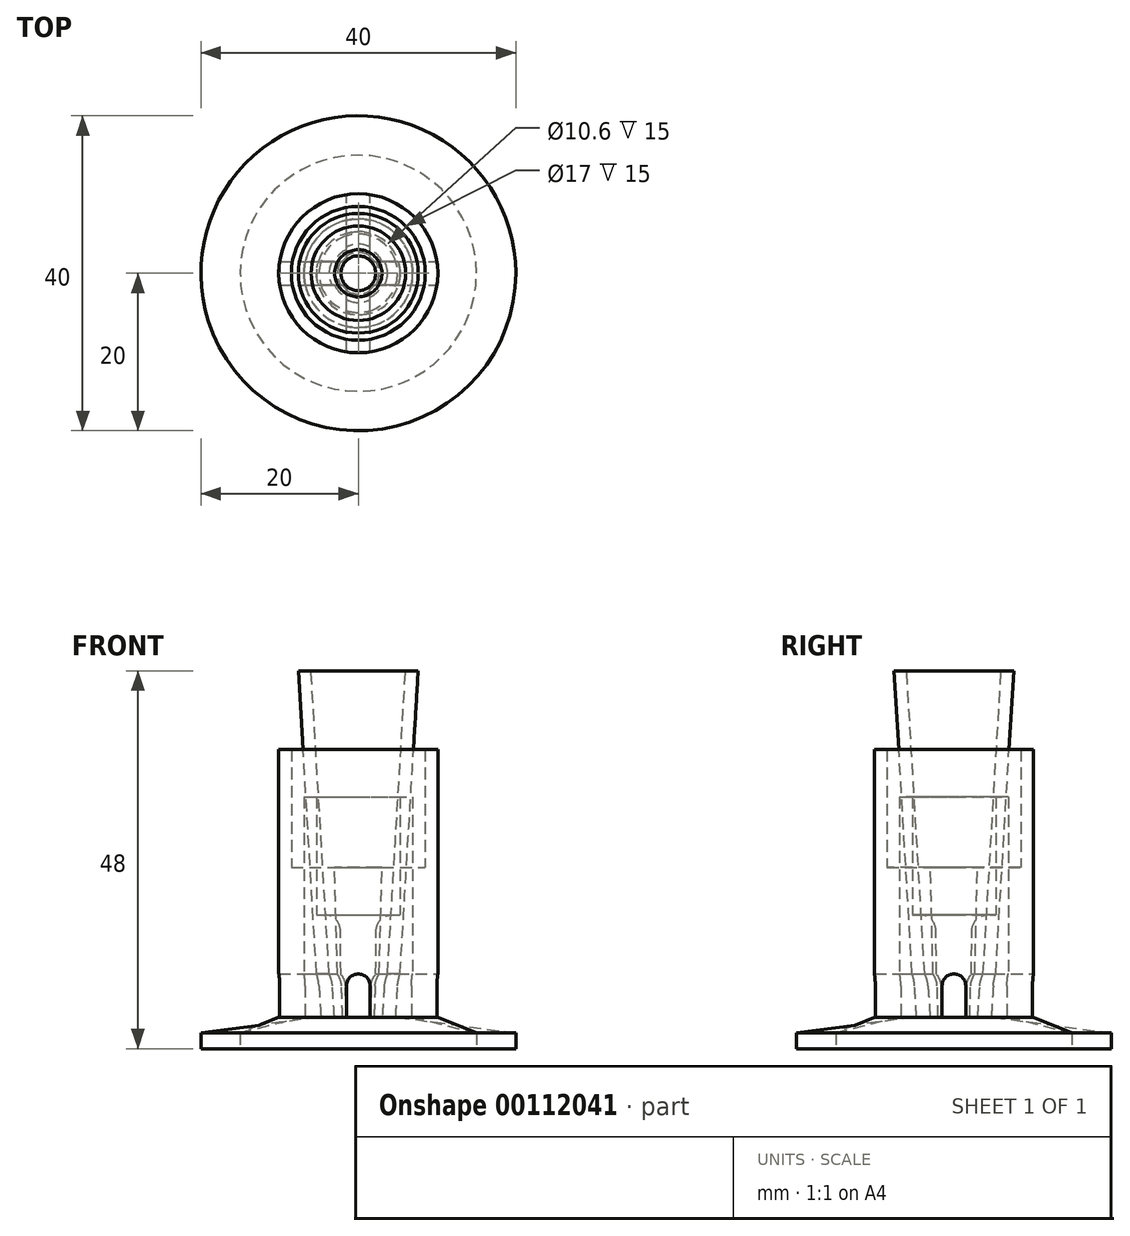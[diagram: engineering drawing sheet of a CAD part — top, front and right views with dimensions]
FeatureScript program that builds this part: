
annotation { "Feature Type Name" : "Feature", "Feature Type Description" : "" }
export const myFeature = defineFeature(function(context is Context, id is Id, definition is map)
    precondition{}
    {
        {
            var Q0;
            Q0=qCreatedBy(makeId("Front.planeOp"),FACE);
            var sketch = newSketch(context, id + "F0", { "sketchPlane" : qUnion([Q0])});
            skLineSegment(sketch, "E0", {"start": v(0, 0) * mm, "end": v(20, 0) * mm});
            skLineSegment(sketch, "E1", {"start": v(20, 0) * mm, "end": v(20, 2) * mm});
            skLineSegment(sketch, "E2", {"start": v(20, 2) * mm, "end": v(4.98, 4) * mm});
            skLineSegment(sketch, "E3", {"start": v(4.98, 4) * mm, "end": v(7.6, 48) * mm});
            skLineSegment(sketch, "E4", {"start": v(7.6, 48) * mm, "end": v(6, 48) * mm});
            skLineSegment(sketch, "E5", {"start": v(6, 48) * mm, "end": v(3.38, 4) * mm});
            skLineSegment(sketch, "E6", {"start": v(3.38, 4) * mm, "end": v(0, 4) * mm});
            skLineSegment(sketch, "E7", {"start": v(0, 4) * mm, "end": v(0, 0) * mm});
            skPoint(sketch, "E8", {"position": v(3.5, 6) * mm});
            skSolve(sketch);
        }
        {
            var Q0;
            Q0 = qSketchRegion(id + "F0", true);
            var Q1;
            Q1=sQuery(id+"F0.wireOp",EDGE,"E7");
            revolve(context, id + "F1", {"entities" : qUnion([Q0]), "axis" : qUnion([Q1]), "revolveType" : RevolveType.FULL});
        }
        {
            var Q0;
            Q0=qCreatedBy(makeId("Front.planeOp"),FACE);
            var sketch = newSketch(context, id + "F2", { "sketchPlane" : qUnion([Q0])});
            skLineSegment(sketch, "E9", {"start": v(1.5, 4) * mm, "end": v(-1.5, 4) * mm});
            skLineSegment(sketch, "E10", {"start": v(-1.5, 4) * mm, "end": v(-1.5, 8) * mm});
            skLineSegment(sketch, "E11", {"start": v(1.5, 4) * mm, "end": v(1.5, 8) * mm});
            skArc(sketch, "E12", {"start": v(1.5, 8) * mm, "mid": v(0, 9.5) * mm, "end": v(-1.5, 8) * mm});
            skSolve(sketch);
        }
        {
            var Q0;
            Q0 = qSketchRegion(id + "F2", true);
            extrude(context, id + "F3", {"entities" : qUnion([Q0]), "endBound" : BoundingType.SYMMETRIC, "depth" : 20 * mm});
        }
        {
            var Q0;
            Q0=makeQuery(id+"F3.opExtrude","SWEPT_BODY",BODY,{"disambiguationData":[OSD([sQuery(id+"F2.wireOp",EDGE,"E9"),sQuery(id+"F2.wireOp",EDGE,"E10"),sQuery(id+"F2.wireOp",EDGE,"E11"),sQuery(id+"F2.wireOp",EDGE,"E12")])]});
            var Q1;
            Q1=makeQuery(id+"F1.opRevolve","SWEPT_EDGE",EDGE,{"disambiguationData":[OSD([sQuery(id+"F0.wireOp",EDGE,"E4"),sQuery(id+"F0.wireOp",EDGE,"E5")])]});
            transform(context, id + "F4", {"entities" : qUnion([Q0]), "transformType" : TransformType.ROTATION, "transformAxis" : qUnion([Q1]), "angle" : 90 * degree, "makeCopy" : true});
        }
        {
            var Q0;
            Q0=makeQuery(id+"F3.opExtrude","SWEPT_BODY",BODY,{"disambiguationData":[OSD([sQuery(id+"F2.wireOp",EDGE,"E9"),sQuery(id+"F2.wireOp",EDGE,"E10"),sQuery(id+"F2.wireOp",EDGE,"E11"),sQuery(id+"F2.wireOp",EDGE,"E12")])]});
            var Q1;
            Q1=makeQuery(id+"F4.opPattern","COPY",BODY,{"derivedFrom":makeQuery(id+"F3.opExtrude","SWEPT_BODY",BODY,{"disambiguationData":[OSD([sQuery(id+"F2.wireOp",EDGE,"E9"),sQuery(id+"F2.wireOp",EDGE,"E10"),sQuery(id+"F2.wireOp",EDGE,"E11"),sQuery(id+"F2.wireOp",EDGE,"E12")])]}),"instanceName":"1"});
            var Q2;
            Q2=makeQuery(id+"F1.opRevolve","SWEPT_BODY",BODY,{"disambiguationData":[OSD([sQuery(id+"F0.wireOp",EDGE,"E0"),sQuery(id+"F0.wireOp",EDGE,"E1"),sQuery(id+"F0.wireOp",EDGE,"E2"),sQuery(id+"F0.wireOp",EDGE,"E3"),sQuery(id+"F0.wireOp",EDGE,"E4"),sQuery(id+"F0.wireOp",EDGE,"E5"),sQuery(id+"F0.wireOp",EDGE,"E6"),sQuery(id+"F0.wireOp",EDGE,"E7")])]});
            booleanBodies(context, id + "F5", {"operationType" : BooleanOperationType.SUBTRACTION, "tools" : qUnion([Q0, Q1]), "targets" : qUnion([Q2])});
        }
        {
            var Q0;
            Q0=qCreatedBy(makeId("Front.planeOp"),FACE);
            var sketch = newSketch(context, id + "F6", { "sketchPlane" : qUnion([Q0])});
            skLineSegment(sketch, "E13", {"start": v(0, 0) * mm, "end": v(0, 4) * mm});
            skLineSegment(sketch, "E14", {"start": v(0, 4) * mm, "end": v(2.5, 4) * mm});
            skLineSegment(sketch, "E15", {"start": v(2.5, 4) * mm, "end": v(3, 23) * mm});
            skLineSegment(sketch, "E16", {"start": v(3, 23) * mm, "end": v(8.5, 23) * mm});
            skLineSegment(sketch, "E17", {"start": v(8.5, 23) * mm, "end": v(8.5, 38) * mm});
            skLineSegment(sketch, "E18", {"start": v(8.5, 38) * mm, "end": v(10.1, 38) * mm});
            skLineSegment(sketch, "E19", {"start": v(10.1, 38) * mm, "end": v(10.1, 4) * mm});
            skLineSegment(sketch, "E20", {"start": v(10.1, 4) * mm, "end": v(15, 2) * mm});
            skLineSegment(sketch, "E21", {"start": v(15, 2) * mm, "end": v(15, 0) * mm});
            skLineSegment(sketch, "E22", {"start": v(15, 0) * mm, "end": v(0, 0) * mm});
            skPoint(sketch, "E23", {"position": v(2.6, 8) * mm});
            skSolve(sketch);
        }
        {
            var Q0;
            Q0 = qSketchRegion(id + "F6", true);
            var Q1;
            Q1=sQuery(id+"F6.wireOp",EDGE,"E13");
            revolve(context, id + "F7", {"entities" : qUnion([Q0]), "axis" : qUnion([Q1]), "revolveType" : RevolveType.FULL});
        }
        {
            var Q0;
            Q0=qCreatedBy(makeId("Front.planeOp"),FACE);
            var sketch = newSketch(context, id + "F8", { "sketchPlane" : qUnion([Q0])});
            skLineSegment(sketch, "E24", {"start": v(-1.5, 8) * mm, "end": v(-1.5, 4) * mm});
            skLineSegment(sketch, "E25", {"start": v(-1.5, 4) * mm, "end": v(1.5, 4) * mm});
            skLineSegment(sketch, "E26", {"start": v(1.5, 4) * mm, "end": v(1.5, 8) * mm});
            skArc(sketch, "E27", {"start": v(1.5, 8) * mm, "mid": v(0, 9.5) * mm, "end": v(-1.5, 8) * mm});
            skSolve(sketch);
        }
        {
            var Q0;
            Q0 = qSketchRegion(id + "F8", true);
            extrude(context, id + "F9", {"entities" : qUnion([Q0]), "endBound" : BoundingType.SYMMETRIC, "depth" : 25 * mm});
        }
        {
            var Q0;
            Q0=makeQuery(id+"F9.opExtrude","SWEPT_BODY",BODY,{"disambiguationData":[OSD([sQuery(id+"F8.wireOp",EDGE,"E24"),sQuery(id+"F8.wireOp",EDGE,"E25"),sQuery(id+"F8.wireOp",EDGE,"E26"),sQuery(id+"F8.wireOp",EDGE,"E27")])]});
            var Q1;
            Q1=makeQuery(id+"F7.opRevolve","SWEPT_EDGE",EDGE,{"disambiguationData":[OSD([sQuery(id+"F6.wireOp",EDGE,"E17"),sQuery(id+"F6.wireOp",EDGE,"E18")])]});
            transform(context, id + "F10", {"entities" : qUnion([Q0]), "transformType" : TransformType.ROTATION, "transformAxis" : qUnion([Q1]), "angle" : 90 * degree, "makeCopy" : true});
        }
        {
            var Q0;
            Q0=makeQuery(id+"F9.opExtrude","SWEPT_BODY",BODY,{"disambiguationData":[OSD([sQuery(id+"F8.wireOp",EDGE,"E24"),sQuery(id+"F8.wireOp",EDGE,"E25"),sQuery(id+"F8.wireOp",EDGE,"E26"),sQuery(id+"F8.wireOp",EDGE,"E27")])]});
            var Q1;
            Q1=makeQuery(id+"F10.opPattern","COPY",BODY,{"derivedFrom":makeQuery(id+"F9.opExtrude","SWEPT_BODY",BODY,{"disambiguationData":[OSD([sQuery(id+"F8.wireOp",EDGE,"E24"),sQuery(id+"F8.wireOp",EDGE,"E25"),sQuery(id+"F8.wireOp",EDGE,"E26"),sQuery(id+"F8.wireOp",EDGE,"E27")])]}),"instanceName":"1"});
            var Q2;
            Q2=makeQuery(id+"F7.opRevolve","SWEPT_BODY",BODY,{"disambiguationData":[OSD([sQuery(id+"F6.wireOp",EDGE,"E13"),sQuery(id+"F6.wireOp",EDGE,"E14"),sQuery(id+"F6.wireOp",EDGE,"E15"),sQuery(id+"F6.wireOp",EDGE,"E16"),sQuery(id+"F6.wireOp",EDGE,"E17"),sQuery(id+"F6.wireOp",EDGE,"E18"),sQuery(id+"F6.wireOp",EDGE,"E19"),sQuery(id+"F6.wireOp",EDGE,"E20"),sQuery(id+"F6.wireOp",EDGE,"E21"),sQuery(id+"F6.wireOp",EDGE,"E22")])]});
            booleanBodies(context, id + "F11", {"operationType" : BooleanOperationType.SUBTRACTION, "tools" : qUnion([Q0, Q1]), "targets" : qUnion([Q2]), "keepTools" : true});
        }
        {
            var Q0;
            Q0=qCreatedBy(makeId("Front.planeOp"),FACE);
            var sketch = newSketch(context, id + "F12", { "sketchPlane" : qUnion([Q0])});
            skLineSegment(sketch, "E28", {"start": v(0, 0) * mm, "end": v(0, 4) * mm});
            skLineSegment(sketch, "E29", {"start": v(0, 4) * mm, "end": v(2.16, 4) * mm});
            skLineSegment(sketch, "E30", {"start": v(2.16, 4) * mm, "end": v(2.28, 15.02) * mm});
            skLineSegment(sketch, "E31", {"start": v(4.28, 17) * mm, "end": v(5.3, 17) * mm});
            skLineSegment(sketch, "E32", {"start": v(5.3, 17) * mm, "end": v(5.3, 32) * mm});
            skLineSegment(sketch, "E33", {"start": v(5.3, 32) * mm, "end": v(6.9, 32) * mm});
            skLineSegment(sketch, "E34", {"start": v(6.9, 32) * mm, "end": v(6.9, 4) * mm});
            skLineSegment(sketch, "E35", {"start": v(6.9, 4) * mm, "end": v(15, 2) * mm});
            skLineSegment(sketch, "E36", {"start": v(15, 2) * mm, "end": v(15, 0) * mm});
            skLineSegment(sketch, "E37", {"start": v(15, 0) * mm, "end": v(0, 0) * mm});
            skPoint(sketch, "E38", {"position": v(2.2, 8) * mm});
            skPoint(sketch, "E39.visualSharp", {"position": v(2.3, 17) * mm});
            skArc(sketch, "E39.filletArc", {"start": v(4.28, 17) * mm, "mid": v(2.87, 16.42) * mm, "end": v(2.28, 15.02) * mm});
            skSolve(sketch);
        }
        {
            var Q0;
            Q0=makeQuery(id+"F12.imprint","IMPRINT",FACE,{"disambiguationData":[TD([[makeQuery(id+"F12.imprint","IMPRINT",EDGE,{"derivedFrom":sQuery(id+"F12.wireOp",EDGE,"E28")}),-1.0]])]});
            var Q1;
            Q1=sQuery(id+"F12.wireOp",EDGE,"E28");
            revolve(context, id + "F13", {"entities" : qUnion([Q0]), "axis" : qUnion([Q1]), "revolveType" : RevolveType.FULL});
        }
        {
            var Q0;
            Q0=makeQuery(id+"F9.opExtrude","SWEPT_BODY",BODY,{"disambiguationData":[OSD([sQuery(id+"F8.wireOp",EDGE,"E24"),sQuery(id+"F8.wireOp",EDGE,"E25"),sQuery(id+"F8.wireOp",EDGE,"E26"),sQuery(id+"F8.wireOp",EDGE,"E27")])]});
            var Q1;
            Q1=makeQuery(id+"F10.opPattern","COPY",BODY,{"derivedFrom":makeQuery(id+"F9.opExtrude","SWEPT_BODY",BODY,{"disambiguationData":[OSD([sQuery(id+"F8.wireOp",EDGE,"E24"),sQuery(id+"F8.wireOp",EDGE,"E25"),sQuery(id+"F8.wireOp",EDGE,"E26"),sQuery(id+"F8.wireOp",EDGE,"E27")])]}),"instanceName":"1"});
            var Q2;
            Q2=makeQuery(id+"F13.opRevolve","SWEPT_BODY",BODY,{"disambiguationData":[OSD([sQuery(id+"F12.wireOp",EDGE,"E28"),sQuery(id+"F12.wireOp",EDGE,"E29"),sQuery(id+"F12.wireOp",EDGE,"E30"),sQuery(id+"F12.wireOp",EDGE,"E31"),sQuery(id+"F12.wireOp",EDGE,"E32"),sQuery(id+"F12.wireOp",EDGE,"E33"),sQuery(id+"F12.wireOp",EDGE,"E34"),sQuery(id+"F12.wireOp",EDGE,"E35"),sQuery(id+"F12.wireOp",EDGE,"E36"),sQuery(id+"F12.wireOp",EDGE,"E37"),sQuery(id+"F12.wireOp",EDGE,"E39.filletArc")])]});
            booleanBodies(context, id + "F14", {"operationType" : BooleanOperationType.SUBTRACTION, "tools" : qUnion([Q0, Q1]), "targets" : qUnion([Q2])});
        }
    });
